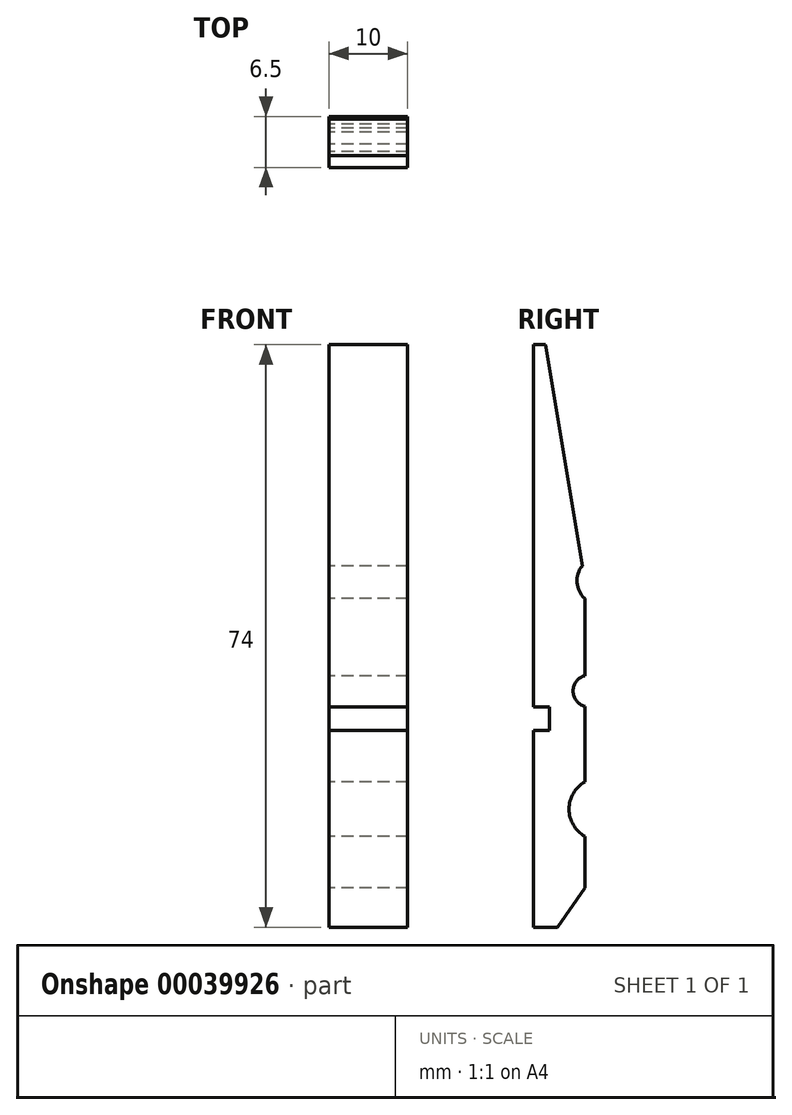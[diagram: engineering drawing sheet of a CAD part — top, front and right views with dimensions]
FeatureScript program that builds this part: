
annotation { "Feature Type Name" : "Feature", "Feature Type Description" : "" }
export const myFeature = defineFeature(function(context is Context, id is Id, definition is map)
    precondition{}
    {
        {
            var Q0;
            Q0=qCreatedBy(makeId("Right.planeOp"),FACE);
            var sketch = newSketch(context, id + "F0", { "sketchPlane" : qUnion([Q0])});
            skLineSegment(sketch, "E0", {"start": v(0, 0) * mm, "end": v(0, 25) * mm});
            skLineSegment(sketch, "E1", {"start": v(0, 25) * mm, "end": v(2, 25) * mm});
            skLineSegment(sketch, "E2", {"start": v(2, 25) * mm, "end": v(2, 28) * mm});
            skLineSegment(sketch, "E3", {"start": v(2, 28) * mm, "end": v(0, 28) * mm});
            skLineSegment(sketch, "E4", {"start": v(0, 28) * mm, "end": v(0, 74) * mm});
            skLineSegment(sketch, "E5", {"start": v(0, 74) * mm, "end": v(1.5, 74) * mm});
            skLineSegment(sketch, "E6", {"start": v(1.5, 74) * mm, "end": v(6.18, 45.9) * mm});
            skLineSegment(sketch, "E7", {"start": v(6.5, 41.76) * mm, "end": v(6.5, 31.94) * mm});
            skArc(sketch, "E8", {"start": v(6.5, 31.94) * mm, "mid": v(5, 30) * mm, "end": v(6.5, 28.06) * mm});
            skLineSegment(sketch, "E9", {"start": v(6.5, 28.06) * mm, "end": v(6.5, 18.46) * mm});
            skLineSegment(sketch, "E10", {"start": v(6.5, 5) * mm, "end": v(3, 0) * mm});
            skLineSegment(sketch, "E11", {"start": v(3, 0) * mm, "end": v(0, 0) * mm});
            skLineSegment(sketch, "E12", {"start": v(6.5, 5) * mm, "end": v(6.5, 11.54) * mm});
            skArc(sketch, "E13", {"start": v(6.5, 18.46) * mm, "mid": v(4.5, 15) * mm, "end": v(6.5, 11.54) * mm});
            skArc(sketch, "E14", {"start": v(6.18, 45.9) * mm, "mid": v(5.5, 43.77) * mm, "end": v(6.5, 41.76) * mm});
            skPoint(sketch, "E15.orphan", {"position": v(6.5, 44) * mm});
            skSolve(sketch);
        }
        {
            var Q0;
            Q0=makeQuery(id+"F0.imprint","IMPRINT",FACE,{"disambiguationData":[TD([[makeQuery(id+"F0.imprint","IMPRINT",EDGE,{"derivedFrom":sQuery(id+"F0.wireOp",EDGE,"E0")}),-1.0]])]});
            extrude(context, id + "F1", {"entities" : qUnion([Q0]), "depth" : 10 * mm});
        }
    });
